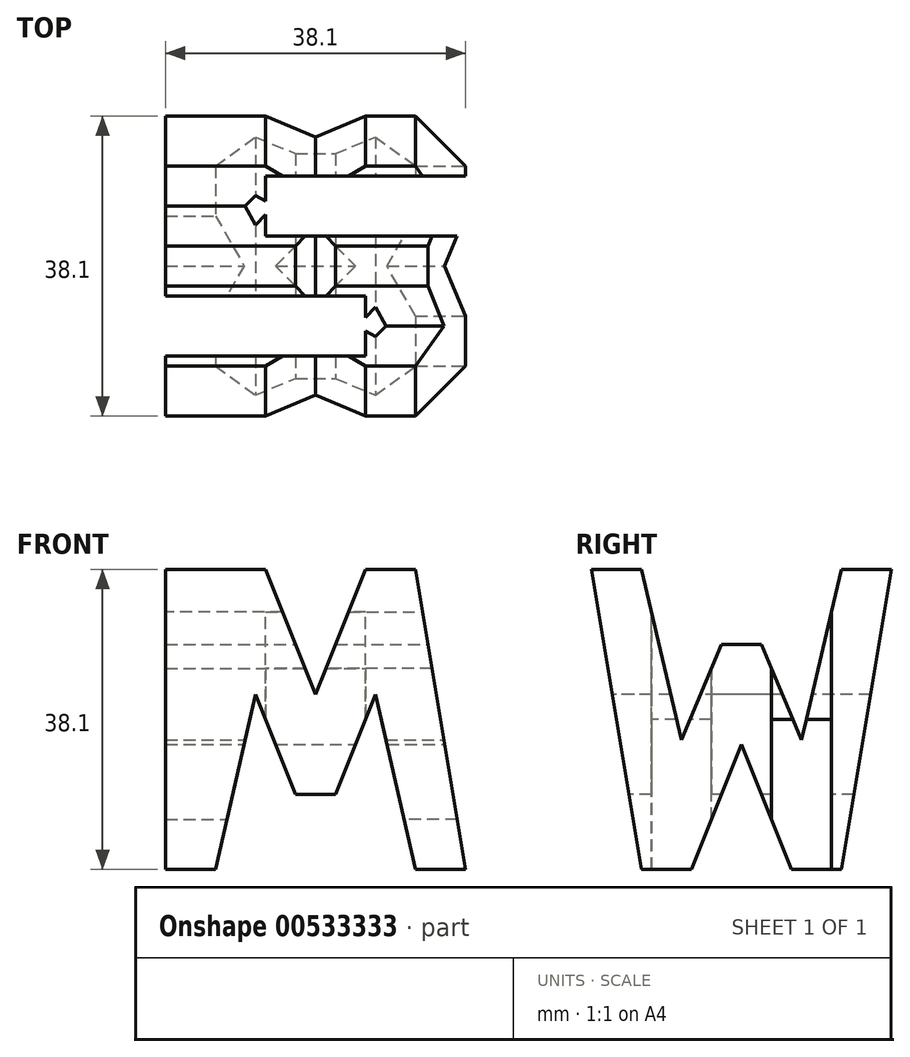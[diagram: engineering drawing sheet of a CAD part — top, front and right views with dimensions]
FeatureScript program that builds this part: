
annotation { "Feature Type Name" : "Feature", "Feature Type Description" : "" }
export const myFeature = defineFeature(function(context is Context, id is Id, definition is map)
    precondition{}
    {
        {
            var Q0;
            Q0=qCreatedBy(makeId("Front.planeOp"),FACE);
            var sketch = newSketch(context, id + "F0", { "sketchPlane" : qUnion([Q0])});
            skLineSegment(sketch, "E0.bottom", {"start": v(38.1, 0) * mm, "end": v(0, 0) * mm});
            skLineSegment(sketch, "E0.top", {"start": v(38.1, 38.1) * mm, "end": v(0, 38.1) * mm});
            skLineSegment(sketch, "E0.left", {"start": v(0, 0) * mm, "end": v(0, 38.1) * mm});
            skLineSegment(sketch, "E0.right", {"start": v(38.1, 0) * mm, "end": v(38.1, 38.1) * mm});
            skSolve(sketch);
        }
        {
            var Q0;
            Q0 = qSketchRegion(id + "F0", true);
            extrude(context, id + "F1", {"entities" : qUnion([Q0]), "depth" : 38.1 * mm, "offsetDistance" : 25.4 * mm});
        }
        {
            var Q0;
            Q0=qCreatedBy(makeId("Front.planeOp"),FACE);
            cPlane(context, id + "F2", {"entities" : qUnion([Q0]), "cplaneType" : CPlaneType.OFFSET, "offset" : 38.1 * mm, "width" : 152.4 * mm, "height" : 152.4 * mm});
        }
        {
            var Q0;
            Q0=qCreatedBy(makeId("Right.planeOp"),FACE);
            cPlane(context, id + "F3", {"entities" : qUnion([Q0]), "cplaneType" : CPlaneType.OFFSET, "offset" : 38.1 * mm, "width" : 152.4 * mm, "height" : 152.4 * mm});
        }
        {
            var Q0;
            Q0=qCreatedBy(makeId("Top.planeOp"),FACE);
            cPlane(context, id + "F4", {"entities" : qUnion([Q0]), "cplaneType" : CPlaneType.OFFSET, "offset" : 38.1 * mm, "width" : 152.4 * mm, "height" : 152.4 * mm});
        }
        {
            var Q0;
            Q0=qCreatedBy(id+"F3.planeOp",FACE);
            var sketch = newSketch(context, id + "F5", { "sketchPlane" : qUnion([Q0])});
            skLineSegment(sketch, "E1.bottom", {"start": v(0, 0) * mm, "end": v(-38.1, 0) * mm});
            skLineSegment(sketch, "E1.top", {"start": v(0, 38.1) * mm, "end": v(-38.1, 38.1) * mm});
            skLineSegment(sketch, "E1.left", {"start": v(0, 0) * mm, "end": v(0, 38.1) * mm});
            skLineSegment(sketch, "E1.right", {"start": v(-38.1, 0) * mm, "end": v(-38.1, 38.1) * mm});
            skLineSegment(sketch, "E2", {"start": v(0, 38.1) * mm, "end": v(-6.35, 0) * mm});
            skLineSegment(sketch, "E3", {"start": v(-38.1, 38.1) * mm, "end": v(-31.75, 0) * mm});
            skLineSegment(sketch, "E4", {"start": v(-31.75, 0) * mm, "end": v(-19.05, 0) * mm});
            skLineSegment(sketch, "E5", {"start": v(-25.4, 0) * mm, "end": v(-19.05, 15.88) * mm});
            skLineSegment(sketch, "E6", {"start": v(-19.05, 15.88) * mm, "end": v(-12.7, 0) * mm});
            skLineSegment(sketch, "E7", {"start": v(-31.75, 38.1) * mm, "end": v(-26.67, 16.45) * mm});
            skLineSegment(sketch, "E8", {"start": v(-26.67, 16.45) * mm, "end": v(-21.6, 28.58) * mm});
            skLineSegment(sketch, "E9", {"start": v(-21.6, 28.58) * mm, "end": v(-16.51, 28.58) * mm});
            skLineSegment(sketch, "E10", {"start": v(-16.51, 28.58) * mm, "end": v(-11.43, 16.45) * mm});
            skLineSegment(sketch, "E11", {"start": v(-11.43, 16.45) * mm, "end": v(-6.35, 38.1) * mm});
            skSolve(sketch);
        }
        {
            var Q0;
            {var subQ0=sQuery(id+"F5.wireOp",EDGE,"E7");Q0=makeQuery(id+"F5.imprint","IMPRINT",FACE,{"disambiguationData":[TD([[makeQuery(id+"F5.imprint","IMPRINT",EDGE,{"derivedFrom":subQ0}),1.0]])]});}
            var Q1;
            {var subQ0=sQuery(id+"F5.wireOp",EDGE,"E1.left");Q1=makeQuery(id+"F5.imprint","IMPRINT",FACE,{"disambiguationData":[TD([[makeQuery(id+"F5.imprint","IMPRINT",EDGE,{"derivedFrom":subQ0}),1.0]])]});}
            var Q2;
            {var subQ4=sQuery(id+"F5.wireOp",EDGE,"E5");Q2=makeQuery(id+"F5.imprint","IMPRINT",FACE,{"disambiguationData":[TD([[makeQuery(id+"F5.imprint","IMPRINT",EDGE,{"derivedFrom":subQ4}),-1.0]])]});}
            var Q3;
            {var subQ0=sQuery(id+"F5.wireOp",EDGE,"E1.right");Q3=makeQuery(id+"F5.imprint","IMPRINT",FACE,{"disambiguationData":[TD([[makeQuery(id+"F5.imprint","IMPRINT",EDGE,{"derivedFrom":subQ0}),-1.0]])]});}
            extrude(context, id + "F6", {"entities" : qUnion([Q0, Q1, Q2, Q3]), "operationType" : NewBodyOperationType.REMOVE, "oppositeDirection" : true, "depth" : 38.1 * mm, "offsetDistance" : 25.4 * mm});
        }
        {
            var Q0;
            Q0=qCreatedBy(id+"F2.planeOp",FACE);
            var sketch = newSketch(context, id + "F7", { "sketchPlane" : qUnion([Q0])});
            skLineSegment(sketch, "E12", {"start": v(0, 0) * mm, "end": v(6.35, 38.1) * mm});
            skLineSegment(sketch, "E13", {"start": v(12.7, 38.1) * mm, "end": v(19.05, 22.23) * mm});
            skLineSegment(sketch, "E14", {"start": v(19.05, 22.23) * mm, "end": v(25.4, 38.1) * mm});
            skLineSegment(sketch, "E15", {"start": v(38.1, 0) * mm, "end": v(31.75, 38.1) * mm});
            skLineSegment(sketch, "E16", {"start": v(6.35, 0) * mm, "end": v(11.43, 22.23) * mm});
            skLineSegment(sketch, "E17", {"start": v(11.43, 22.23) * mm, "end": v(16.51, 9.52) * mm});
            skLineSegment(sketch, "E18", {"start": v(16.51, 9.53) * mm, "end": v(21.6, 9.53) * mm});
            skLineSegment(sketch, "E19", {"start": v(21.6, 9.53) * mm, "end": v(26.67, 22.23) * mm});
            skLineSegment(sketch, "E20", {"start": v(26.67, 22.23) * mm, "end": v(31.75, 0) * mm});
            skLineSegment(sketch, "E21.bottom", {"start": v(0, 0) * mm, "end": v(38.1, 0) * mm});
            skLineSegment(sketch, "E21.top", {"start": v(6.35, 38.1) * mm, "end": v(38.1, 38.1) * mm});
            skLineSegment(sketch, "E21.right", {"start": v(38.1, 0) * mm, "end": v(38.1, 38.1) * mm});
            skLineSegment(sketch, "E22", {"start": v(6.35, 38.1) * mm, "end": v(0, 0) * mm});
            skLineSegment(sketch, "E23", {"start": v(0, 0) * mm, "end": v(0, 38.1) * mm});
            skLineSegment(sketch, "E24", {"start": v(0, 38.1) * mm, "end": v(6.35, 38.1) * mm});
            skSolve(sketch);
        }
        {
            var Q0;
            {var subQ0=sQuery(id+"F7.wireOp",EDGE,"E16");Q0=makeQuery(id+"F7.imprint","IMPRINT",FACE,{"disambiguationData":[TD([[makeQuery(id+"F7.imprint","IMPRINT",EDGE,{"derivedFrom":subQ0}),-1.0]])]});}
            var Q1;
            {var subQ0=sQuery(id+"F7.wireOp",EDGE,"E13");Q1=makeQuery(id+"F7.imprint","IMPRINT",FACE,{"disambiguationData":[TD([[makeQuery(id+"F7.imprint","IMPRINT",EDGE,{"derivedFrom":subQ0}),1.0]])]});}
            var Q2;
            {var subQ0=sQuery(id+"F7.wireOp",EDGE,"E15");Q2=makeQuery(id+"F7.imprint","IMPRINT",FACE,{"disambiguationData":[TD([[makeQuery(id+"F7.imprint","IMPRINT",EDGE,{"derivedFrom":subQ0}),-1.0]])]});}
            var Q3;
            Q3=makeQuery(id+"F7.imprint","IMPRINT",FACE,{"disambiguationData":[TD([[makeQuery(id+"F7.imprint","IMPRINT",EDGE,{"derivedFrom":sQuery(id+"F7.wireOp",EDGE,"E22")}),-1.0]])]});
            extrude(context, id + "F8", {"entities" : qUnion([Q0, Q1, Q2, Q3]), "operationType" : NewBodyOperationType.REMOVE, "oppositeDirection" : true, "depth" : 38.1 * mm, "offsetDistance" : 25.4 * mm});
        }
        {
            var Q0;
            Q0=qCreatedBy(id+"F4.planeOp",FACE);
            var sketch = newSketch(context, id + "F9", { "sketchPlane" : qUnion([Q0])});
            skLineSegment(sketch, "E25", {"start": v(38.1, -38.1) * mm, "end": v(38.1, 0) * mm});
            skLineSegment(sketch, "E26", {"start": v(38.1, 0) * mm, "end": v(0, 0) * mm});
            skLineSegment(sketch, "E27", {"start": v(0, 0) * mm, "end": v(0, -38.1) * mm});
            skLineSegment(sketch, "E28", {"start": v(0, -38.1) * mm, "end": v(38.1, -38.1) * mm});
            skLineSegment(sketch, "E29", {"start": v(0, -30.48) * mm, "end": v(25.4, -30.48) * mm});
            skLineSegment(sketch, "E30", {"start": v(25.4, -30.48) * mm, "end": v(25.4, -22.86) * mm});
            skLineSegment(sketch, "E31", {"start": v(25.4, -22.86) * mm, "end": v(0, -22.86) * mm});
            skLineSegment(sketch, "E32", {"start": v(38.1, -7.62) * mm, "end": v(12.7, -7.62) * mm});
            skLineSegment(sketch, "E33", {"start": v(12.7, -7.62) * mm, "end": v(12.7, -15.24) * mm});
            skLineSegment(sketch, "E34", {"start": v(12.7, -15.24) * mm, "end": v(38.1, -15.24) * mm});
            skSolve(sketch);
        }
        {
            var Q0;
            {var subQ0=sQuery(id+"F9.wireOp",EDGE,"E29");Q0=makeQuery(id+"F9.imprint","IMPRINT",FACE,{"disambiguationData":[TD([[makeQuery(id+"F9.imprint","IMPRINT",EDGE,{"derivedFrom":subQ0}),1.0]])]});}
            var Q1;
            {var subQ0=sQuery(id+"F9.wireOp",EDGE,"E32");Q1=makeQuery(id+"F9.imprint","IMPRINT",FACE,{"disambiguationData":[TD([[makeQuery(id+"F9.imprint","IMPRINT",EDGE,{"derivedFrom":subQ0}),1.0]])]});}
            extrude(context, id + "F10", {"entities" : qUnion([Q0, Q1]), "operationType" : NewBodyOperationType.REMOVE, "oppositeDirection" : true, "depth" : 38.1 * mm, "offsetDistance" : 25.4 * mm});
        }
    });
